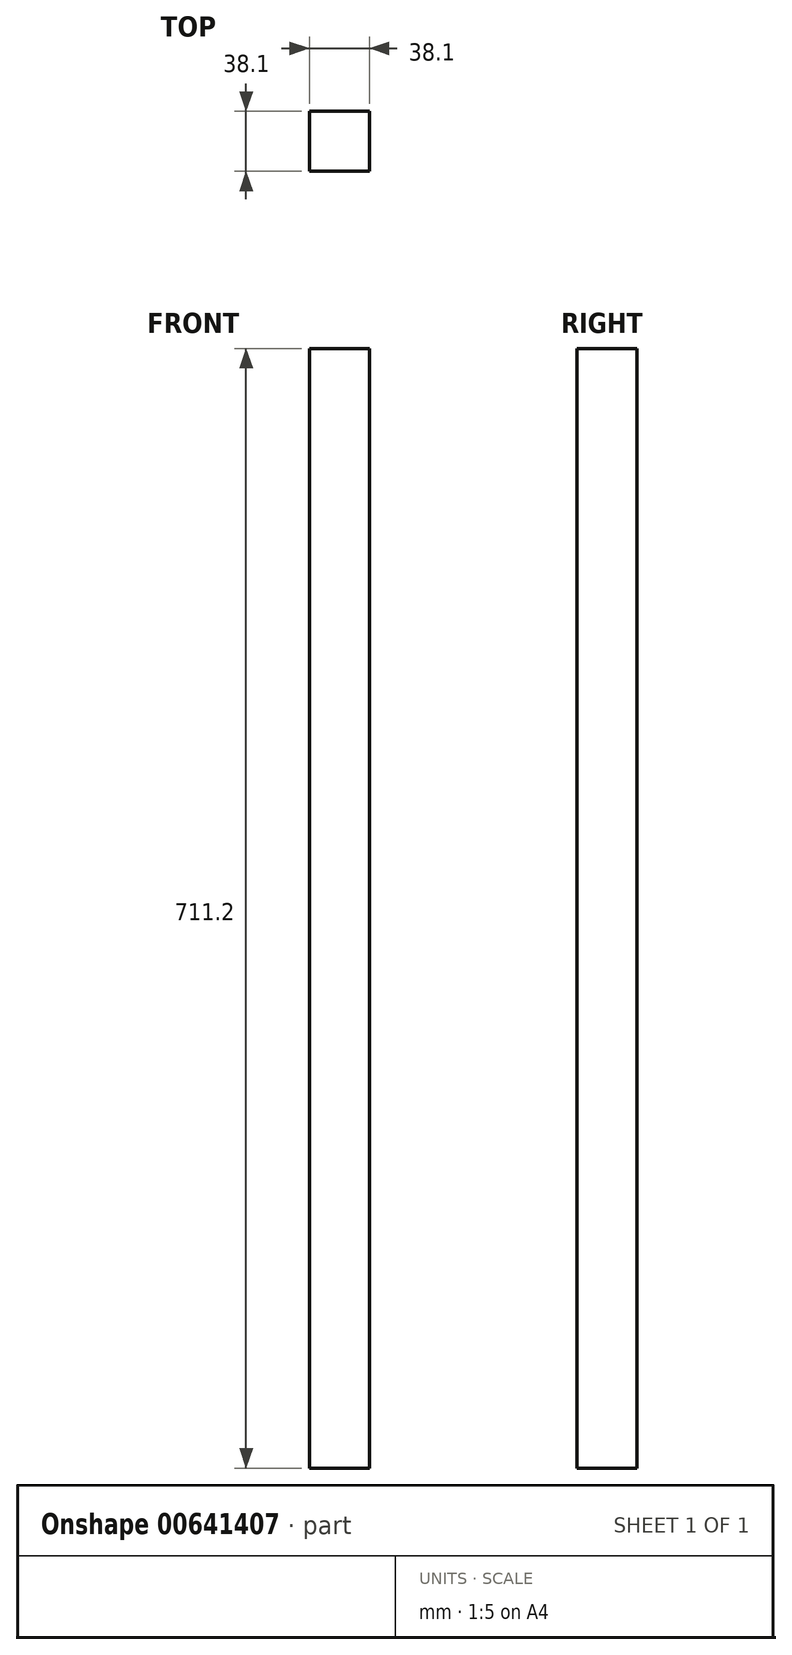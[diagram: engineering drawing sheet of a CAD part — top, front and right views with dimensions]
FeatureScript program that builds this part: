
annotation { "Feature Type Name" : "Feature", "Feature Type Description" : "" }
export const myFeature = defineFeature(function(context is Context, id is Id, definition is map)
    precondition{}
    {
        {
            var Q0;
            Q0=qCreatedBy(makeId("Front.planeOp"),FACE);
            var sketch = newSketch(context, id + "F0", { "sketchPlane" : qUnion([Q0])});
            skLineSegment(sketch, "E0.bottom", {"start": v(-19.05, -355.6) * mm, "end": v(19.05, -355.6) * mm});
            skLineSegment(sketch, "E0.top", {"start": v(-19.05, 355.6) * mm, "end": v(19.05, 355.6) * mm});
            skLineSegment(sketch, "E0.left", {"start": v(-19.05, -355.6) * mm, "end": v(-19.05, 355.6) * mm});
            skLineSegment(sketch, "E0.right", {"start": v(19.05, -355.6) * mm, "end": v(19.05, 355.6) * mm});
            skPoint(sketch, "E0.middle", {"position": v(0, 0) * mm});
            skSolve(sketch);
        }
        {
            var Q0;
            Q0 = qSketchRegion(id + "F0", true);
            extrude(context, id + "F1", {"entities" : qUnion([Q0]), "endBound" : BoundingType.SYMMETRIC, "depth" : 38.1 * mm, "offsetDistance" : 25.4 * mm});
        }
    });
